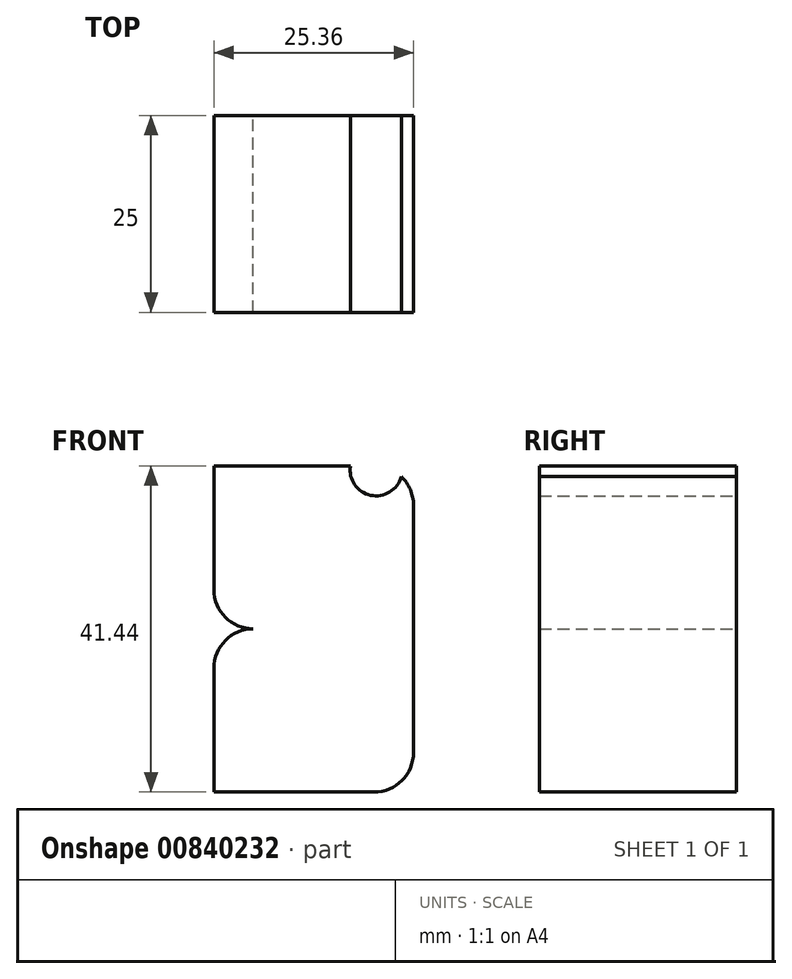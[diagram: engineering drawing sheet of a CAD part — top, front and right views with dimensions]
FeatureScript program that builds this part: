
annotation { "Feature Type Name" : "Feature", "Feature Type Description" : "" }
export const myFeature = defineFeature(function(context is Context, id is Id, definition is map)
    precondition{}
    {
        {
            var Q0;
            Q0=qCreatedBy(makeId("Front.planeOp"),FACE);
            var sketch = newSketch(context, id + "F0", { "sketchPlane" : qUnion([Q0])});
            skLineSegment(sketch, "E0.bottom", {"start": v(5, 0) * mm, "end": v(25.36, 0) * mm});
            skLineSegment(sketch, "E0.top", {"start": v(0, 20.72) * mm, "end": v(20.36, 20.72) * mm});
            skLineSegment(sketch, "E0.left", {"start": v(0, 5) * mm, "end": v(0, 20.72) * mm});
            skLineSegment(sketch, "E0.right", {"start": v(25.36, 0) * mm, "end": v(25.36, 15.72) * mm});
            skPoint(sketch, "E1.visualSharp", {"position": v(25.36, 20.72) * mm});
            skArc(sketch, "E1.filletArc", {"start": v(25.36, 15.72) * mm, "mid": v(23.9, 19.26) * mm, "end": v(20.36, 20.72) * mm});
            skPoint(sketch, "E2.visualSharp", {"position": v(0, 0) * mm});
            skArc(sketch, "E2.filletArc", {"start": v(0, 5) * mm, "mid": v(1.46, 1.46) * mm, "end": v(5, 0) * mm});
            skSolve(sketch);
        }
        {
            var Q0;
            Q0 = qSketchRegion(id + "F0", true);
            extrude(context, id + "F1", {"entities" : qUnion([Q0]), "depth" : 25 * mm, "offsetDistance" : 25 * mm});
        }
        {
            var Q0;
            Q0=makeQuery(id+"F1.opExtrude","SWEPT_BODY",BODY,{"disambiguationData":[OSD([sQuery(id+"F0.wireOp",EDGE,"E0.bottom"),sQuery(id+"F0.wireOp",EDGE,"E0.top"),sQuery(id+"F0.wireOp",EDGE,"E0.left"),sQuery(id+"F0.wireOp",EDGE,"E0.right"),sQuery(id+"F0.wireOp",EDGE,"E1.filletArc"),sQuery(id+"F0.wireOp",EDGE,"E2.filletArc")])]});
            var Q1;
            Q1=makeQuery(id+"F1.opExtrude","SWEPT_FACE",FACE,{"disambiguationData":[OSD([sQuery(id+"F0.wireOp",EDGE,"E0.bottom")])]});
            mirror(context, id + "F2", {"operationType" : NewBodyOperationType.ADD, "entities" : qUnion([Q0]), "mirrorPlane" : qUnion([Q1])});
        }
        {
            var Q0;
            {var subQ0=makeQuery(id+"F1.opExtrude","CAP_FACE",FACE,{"disambiguationData":[OSD([sQuery(id+"F0.wireOp",EDGE,"E0.bottom"),sQuery(id+"F0.wireOp",EDGE,"E0.top"),sQuery(id+"F0.wireOp",EDGE,"E0.left"),sQuery(id+"F0.wireOp",EDGE,"E0.right"),sQuery(id+"F0.wireOp",EDGE,"E1.filletArc"),sQuery(id+"F0.wireOp",EDGE,"E2.filletArc")])],"isStart":true});Q0=makeQuery(id+"F2.boolean.opBoolean","MERGE",FACE,{"derivedFrom":[subQ0,makeQuery(id+"F2.opPattern","COPY",FACE,{"derivedFrom":subQ0,"instanceName":"1"})]});}
            var sketch = newSketch(context, id + "F3", { "sketchPlane" : qUnion([Q0])});
            skCircle(sketch, "E3", {"center": v(-20.6, 20.21) * mm, "radius": 3.31 * mm});
            skSolve(sketch);
        }
        {
            var Q0;
            Q0=makeQuery(id+"F3.imprint","IMPRINT",FACE,{"disambiguationData":[TD([[makeQuery(id+"F3.imprint","IMPRINT",EDGE,{"derivedFrom":sQuery(id+"F3.wireOp",EDGE,"E3")}),1.0]])]});
            var Q1;
            Q1=sQuery(id+"F3.wireOp",EDGE,"E3");
            extrude(context, id + "F4", {"entities" : qUnion([Q0]), "operationType" : NewBodyOperationType.REMOVE, "surfaceOperationType" : NewSurfaceOperationType.ADD, "surfaceEntities" : qUnion([Q1]), "oppositeDirection" : true, "depth" : 25 * mm, "offsetDistance" : 25 * mm});
        }
    });
